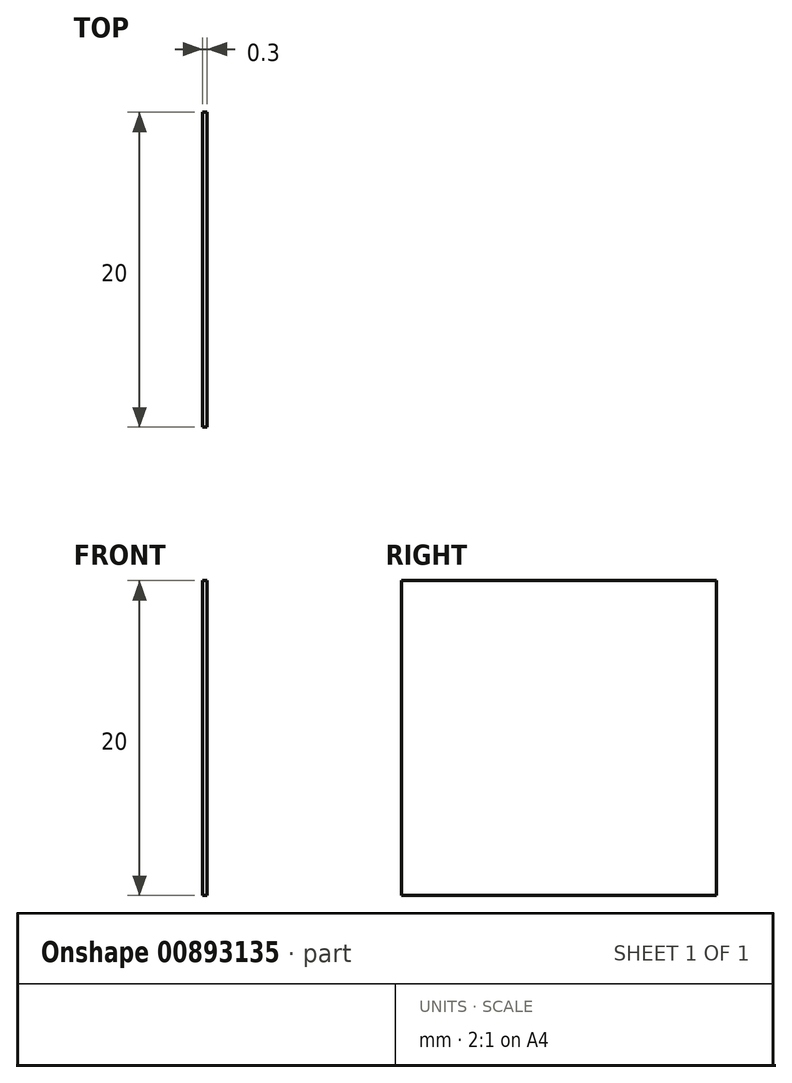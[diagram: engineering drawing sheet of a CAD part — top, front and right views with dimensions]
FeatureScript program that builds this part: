
annotation { "Feature Type Name" : "Feature", "Feature Type Description" : "" }
export const myFeature = defineFeature(function(context is Context, id is Id, definition is map)
    precondition{}
    {
        {
            var Q0;
            Q0=qCreatedBy(makeId("Right.planeOp"),FACE);
            var sketch = newSketch(context, id + "F0", { "sketchPlane" : qUnion([Q0])});
            skLineSegment(sketch, "E0.bottom", {"start": v(0, 0) * mm, "end": v(20, 0) * mm});
            skLineSegment(sketch, "E0.top", {"start": v(0, -20) * mm, "end": v(20, -20) * mm});
            skLineSegment(sketch, "E0.left", {"start": v(0, 0) * mm, "end": v(0, -20) * mm});
            skLineSegment(sketch, "E0.right", {"start": v(20, 0) * mm, "end": v(20, -20) * mm});
            skSolve(sketch);
        }
        {
            var Q0;
            Q0=makeQuery(id+"F0.imprint","IMPRINT",FACE,{"disambiguationData":[TD([[makeQuery(id+"F0.imprint","IMPRINT",EDGE,{"derivedFrom":sQuery(id+"F0.wireOp",EDGE,"E0.bottom")}),-1.0]])]});
            extrude(context, id + "F1", {"entities" : qUnion([Q0]), "depth" : .30 * mm, "offsetDistance" : 25 * mm});
        }
    });
